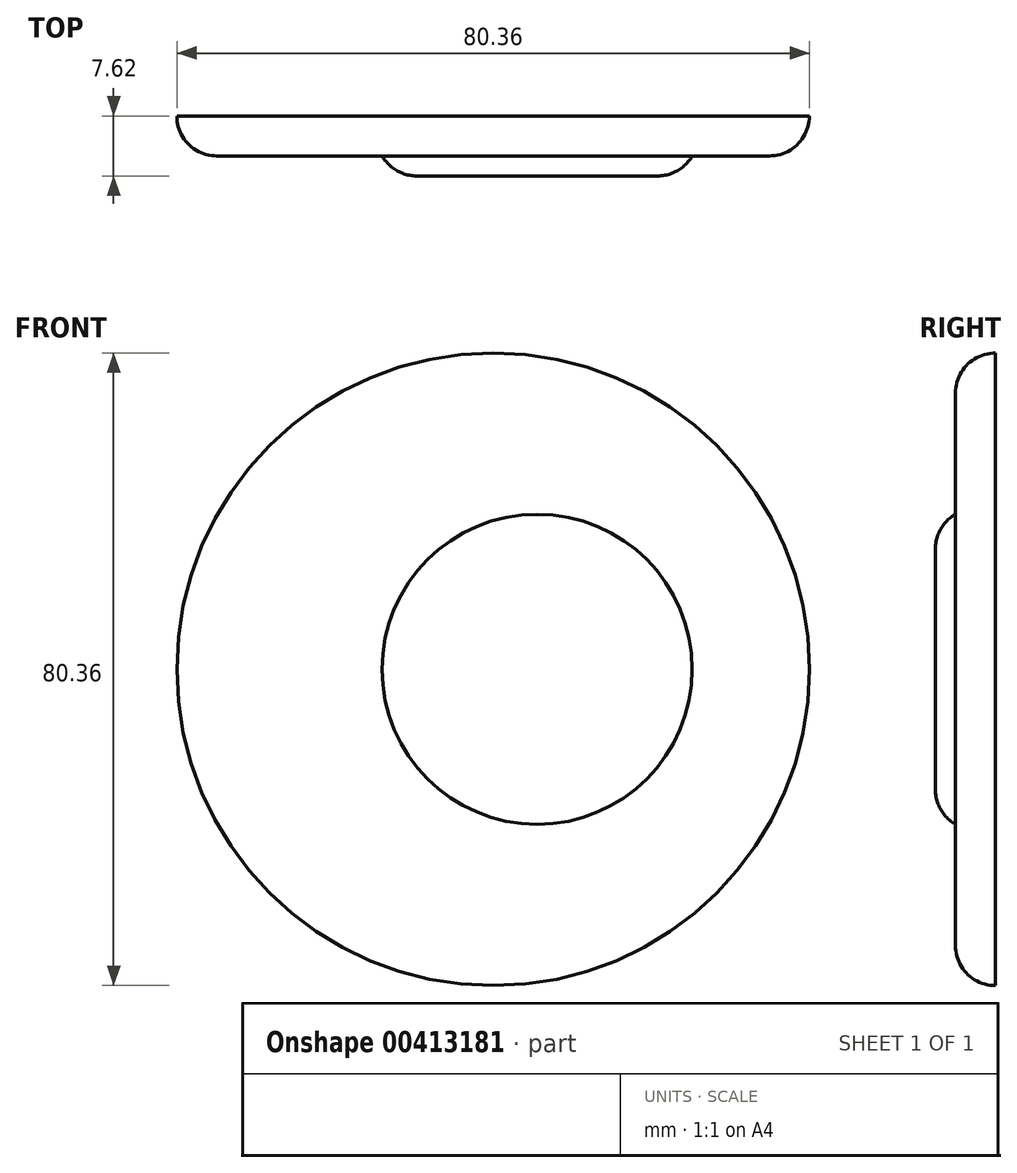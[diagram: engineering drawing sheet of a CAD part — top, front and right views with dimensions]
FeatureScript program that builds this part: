
annotation { "Feature Type Name" : "Feature", "Feature Type Description" : "" }
export const myFeature = defineFeature(function(context is Context, id is Id, definition is map)
    precondition{}
    {
        {
            var Q0;
            Q0=qCreatedBy(makeId("Front.planeOp"),FACE);
            var sketch = newSketch(context, id + "F0", { "sketchPlane" : qUnion([Q0])});
            skCircle(sketch, "E0", {"center": v(0, 0) * mm, "radius": 40.18 * mm});
            skSolve(sketch);
        }
        {
            var Q0;
            Q0 = qSketchRegion(id + "F0", true);
            extrude(context, id + "F1", {"entities" : qUnion([Q0]), "depth" : 5.08 * mm});
        }
        {
            var Q0;
            Q0=makeQuery(id+"F1.opExtrude","CAP_FACE",FACE,{"disambiguationData":[OSD([sQuery(id+"F0.wireOp",EDGE,"E0")])],"isStart":false});
            var sketch = newSketch(context, id + "F2", { "sketchPlane" : qUnion([Q0])});
            skCircle(sketch, "E1", {"center": v(5.59, 0) * mm, "radius": 19.7 * mm});
            skSolve(sketch);
        }
        {
            var Q0;
            Q0 = qSketchRegion(id + "F2", true);
            extrude(context, id + "F3", {"entities" : qUnion([Q0]), "operationType" : NewBodyOperationType.ADD, "depth" : 2.54 * mm});
        }
        {
            var Q0;
            Q0=makeQuery(id+"F1.opExtrude","CAP_EDGE",EDGE,{"disambiguationData":[OSD([sQuery(id+"F0.wireOp",EDGE,"E0")])],"isStart":false});
            fillet(context, id + "F4", {"entities" : qUnion([Q0]), "radius" : 5.08 * mm, "tangentPropagation" : true, "allowEdgeOverflow" : false});
        }
        {
            var Q0;
            Q0=makeQuery(id+"F3.opExtrude","CAP_EDGE",EDGE,{"disambiguationData":[OSD([sQuery(id+"F2.wireOp",EDGE,"E1")])],"isStart":false});
            fillet(context, id + "F5", {"entities" : qUnion([Q0]), "radius" : 5.08 * mm, "tangentPropagation" : true, "allowEdgeOverflow" : false});
        }
    });
